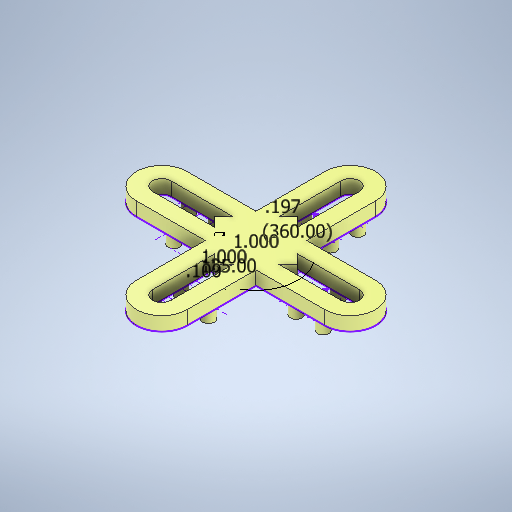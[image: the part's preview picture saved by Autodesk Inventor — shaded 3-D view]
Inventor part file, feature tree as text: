
AUTODESK INVENTOR PART (.ipt)
format: ipt  version: 2025.1 (Build 291241000, 241)  size: 441,344 bytes
history: native  units: in
note: dims shown in document units (in); Inventor stores cm internally (conversion verified against a paired STEP export)
features: sketch x6, extrude x4, other x1
ambient origin geometry x8: Origin, YZ Plane, XZ Plane, XY Plane, X Axis, Y Axis, Z Axis, Center Point
bodies: Solid1 (feature_tree)
feature tree (11):
  sketch  "Sketch1"  dims[d12=1.0in d15=1.0in]
  extrude  "Extrusion1"  Depth=1.0in
  extrude  "Extrusion2"  TaperAngle=135.0deg  [1 undecoded]
  extrude  "Extrusion3"  Depth=0.1969in TaperAngle=360.0deg
  extrude  "Extrusion4"  Depth=0.2205in TaperAngle=0.0deg
  sketch  "Sketch Circular Pattern1"  dims[d18=0.1in d19=135.0deg]
  sketch  "Sketch2"  dims[d25=0.1969in d39=1.5748in d41=360.0deg]
  sketch  "Sketch Circular Pattern2"  dims[d43=0.2362in d44=0.0in d45=0.2205in d46=0.0in]
  sketch  "Sketch3"  dims[d47=0.2067in]
  sketch  "Sketch Circular Pattern3"  dims[d48=0.2067in d49=0.2067in d50=1.5748in d52=360.0deg d54=0.0236in d55=0.0in d56=0.1575in d57=0.1575in d58=0.1575in d59=1.5748in d61=360.0deg d63=0.2362in d64=0.0in]
  other  "Finish1"
note: 1 required parameter value undecoded (feature->parameter linkage not recoverable at this tier; creation-order binding heuristic only, values carry confidence <= 0.55)
